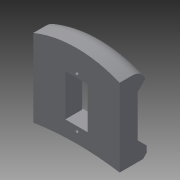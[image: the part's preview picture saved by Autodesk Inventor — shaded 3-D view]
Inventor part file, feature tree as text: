
AUTODESK INVENTOR PART (.ipt)
format: ipt  version: 2015 (Build 190159000, 159)  size: 159,744 bytes
history: native  units: mm
features: extrude x3, fillet x3, sketch x3, chamfer x2
ambient origin geometry x8: Origin, YZ Plane, XZ Plane, XY Plane, X Axis, Y Axis, Z Axis, Center Point
bodies: Solid1 (feature_tree)
feature tree (11):
  extrude  "Extrusion1"  Depth=23.2mm
  extrude  "Extrusion2"  Depth=15.0mm TaperAngle=0.0deg
  extrude  "Extrusion3"  Depth=2.35mm
  fillet  "Fillet1"  Radius=2.0mm
  chamfer  "Chamfer1"  Distance=2.35mm
  chamfer  "Chamfer2"  Distance=2.0mm
  fillet  "Fillet2"  Radius=5.0mm
  fillet  "Fillet3"  Radius=8.0mm
  sketch  "Sketch1"  dims[d6=150.0mm d7=23.2mm]
  sketch  "Sketch2"  dims[d8=12.4mm d9=15.0mm d10=0.0mm]
  sketch  "Sketch3"  dims[d11=5.0mm d12=0.0mm d13=2.35mm d14=2.0mm d15=2.35mm d16=2.0mm d17=5.0mm d18=0.0mm d19=8.0mm d20=5.0mm d21=2.0mm d22=45.0deg d23=2.0mm d24=2.0mm d25=45.0deg d26=1.0mm d27=1.0mm]
